# Revit family: Bügelschellen für Schirmanschluss
name_source: partatom
category: Generic Models
revit_build: Autodesk Revit 2015 (Build: 20140606_1530(x64)
units: mm (PartAtom-declared; Revit-internal decimal feet)

## types (5) — shared parameters
Length = 20 mm  [stored 0.0656168 ft]
Manufacturer = OBO Bettermann
Material = Stainless Steel
URL = http://www.obo-bettermann.com

## per-type parameters (varying)
| type | Article Type | GTIN | Height | Height 1 | Height 2 | Height 3 | Height 4 | Height 5 | Manufacturer Art.No. | Radius | Width |
| 2056N SAS 8 VA | 2056N SAS 8 VA | 4012195432371 | 30 mm  [stored 0.0984252 ft] | 26 mm | 1 mm  [stored 0.00328084 ft] | 5 mm  [stored 0.0164042 ft] | 4 mm  [stored 0.0131234 ft] | 2 mm  [stored 0.00656168 ft] | 1167006 | 4 mm  [stored 0.0131234 ft] | 12 mm  [stored 0.0393701 ft] |
| 2056N SAS 12VA | 2056N SAS 12 VA | 4012195432432 | 34 mm | 30 mm  [stored 0.0984252 ft] | 2 mm  [stored 0.00656168 ft] | 5 mm  [stored 0.0164042 ft] | 7 mm  [stored 0.0229659 ft] | 1 mm  [stored 0.00328084 ft] | 1167014 | 6 mm  [stored 0.019685 ft] | 17 mm |
| 2056N SAS 16VA | 2056N SAS 16 VA | 4012195432494 | 38 mm  [stored 0.124672 ft] | 34 mm | 3 mm  [stored 0.00984252 ft] | 7 mm  [stored 0.0229659 ft] | 9 mm  [stored 0.0295276 ft] | 2 mm  [stored 0.00656168 ft] | 1167022 | 8 mm  [stored 0.0262467 ft] | 20 mm  [stored 0.0656168 ft] |
| 2056N SAS 22 VA | 2056N SAS 22 VA | 4012195432555 | 44 mm  [stored 0.144357 ft] | 40 mm | 4 mm  [stored 0.0131234 ft] | 8 mm  [stored 0.0262467 ft] | 10 mm  [stored 0.0328084 ft] | 4 mm  [stored 0.0131234 ft] | 1167030 | 11 mm  [stored 0.0360892 ft] | 27 mm  [stored 0.0885827 ft] |
| 2056N SAS 28 VA | 2056N SAS 28 VA | 4012195432616 | 51 mm | 47 mm | 5 mm  [stored 0.0164042 ft] | 9 mm  [stored 0.0295276 ft] | 11 mm  [stored 0.0360892 ft] | 6 mm  [stored 0.019685 ft] | 1167049 | 15 mm  [stored 0.0492126 ft] | 33 mm  [stored 0.108268 ft] |

note: [stored X ft] marks values corroborated as IEEE doubles in the binary element streams (Revit-internal decimal feet)

## geometry (parser evidence)
native form markers: Sweep x2
no freeform markers — native parametric forms only
